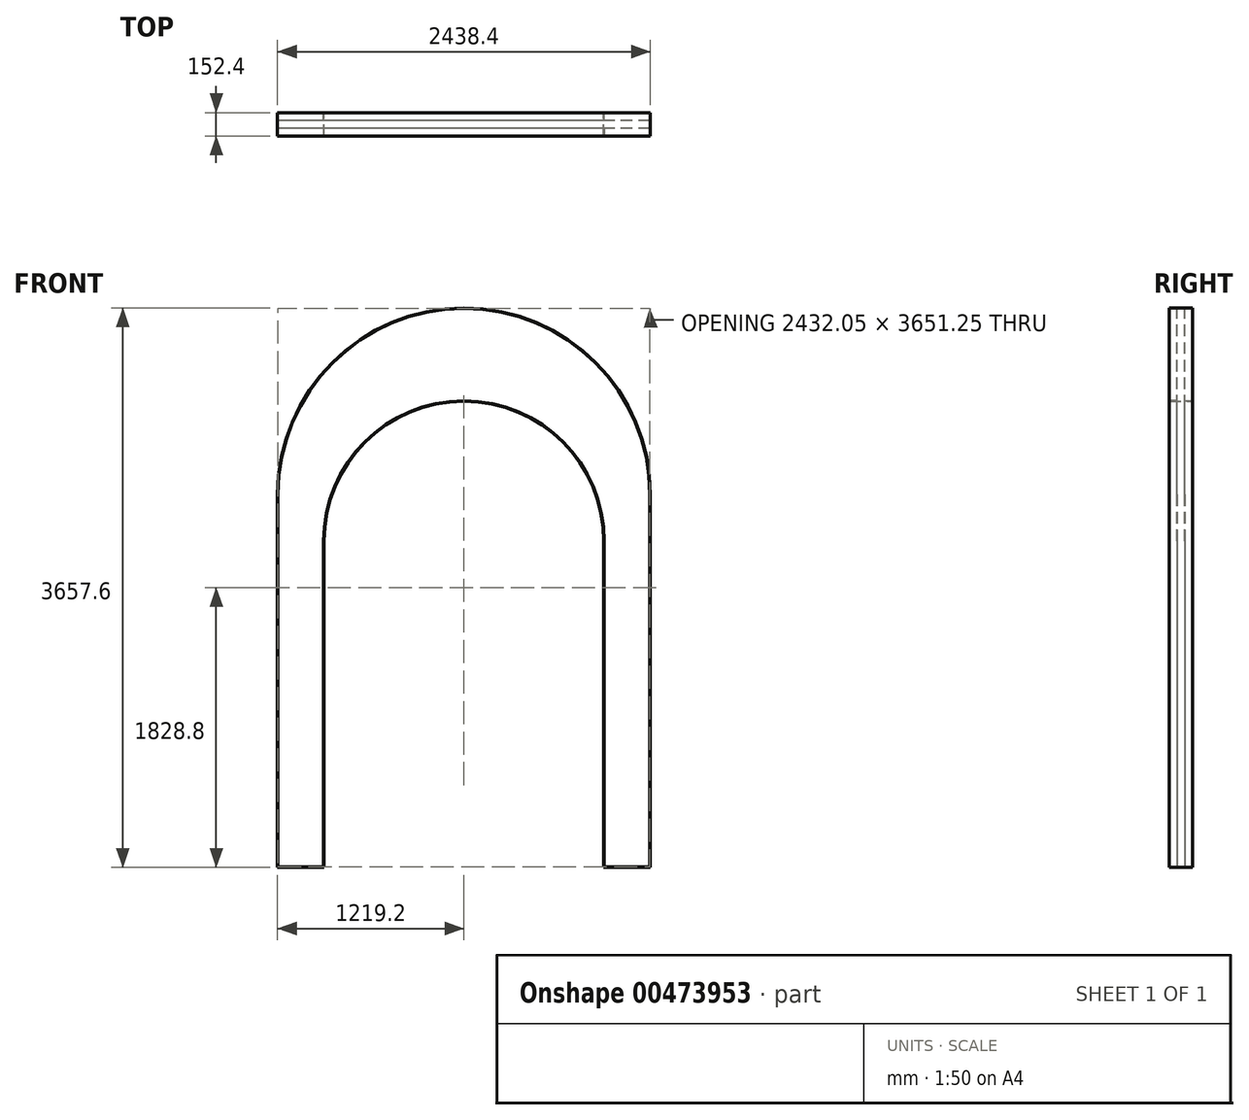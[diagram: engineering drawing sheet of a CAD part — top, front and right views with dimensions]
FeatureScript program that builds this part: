
annotation { "Feature Type Name" : "Feature", "Feature Type Description" : "" }
export const myFeature = defineFeature(function(context is Context, id is Id, definition is map)
    precondition{}
    {
        {
            var Q0;
            Q0=qCreatedBy(makeId("Front.planeOp"),FACE);
            var sketch = newSketch(context, id + "F0", { "sketchPlane" : qUnion([Q0])});
            skLineSegment(sketch, "E0", {"start": v(-1219.2, 0) * mm, "end": v(-1219.2, 2438.4) * mm});
            skLineSegment(sketch, "E1", {"start": v(1219.2, 2438.4) * mm, "end": v(1219.2, 0) * mm});
            skLineSegment(sketch, "E2", {"start": v(1219.2, 0) * mm, "end": v(0, 0) * mm});
            skLineSegment(sketch, "E3", {"start": v(0, 0) * mm, "end": v(-1219.2, 0) * mm});
            skArc(sketch, "E4", {"start": v(-1219.2, 2438.4) * mm, "mid": v(0, 3657.6) * mm, "end": v(1219.2, 2438.4) * mm});
            skLineSegment(sketch, "E5", {"start": v(-914.4, 0) * mm, "end": v(-914.4, 2133.6) * mm});
            skArc(sketch, "E6", {"start": v(914.4, 2133.6) * mm, "mid": v(0, 3048) * mm, "end": v(-914.4, 2133.6) * mm});
            skLineSegment(sketch, "E7", {"start": v(914.4, 2133.6) * mm, "end": v(914.4, 0) * mm});
            skSolve(sketch);
        }
        {
            var Q0;
            {var subQ4=sQuery(id+"F0.wireOp",EDGE,"E0");Q0=makeQuery(id+"F0.imprint","IMPRINT",FACE,{"disambiguationData":[TD([[makeQuery(id+"F0.imprint","IMPRINT",EDGE,{"derivedFrom":subQ4}),-1.0]])]});}
            extrude(context, id + "F1", {"entities" : qUnion([Q0]), "depth" : 76.2 * mm, "offsetDistance" : 25.4 * mm});
        }
        {
            var Q0;
            Q0=makeQuery(id+"F1.opExtrude","CAP_FACE",FACE,{"disambiguationData":[OSD([sQuery(id+"F0.wireOp",EDGE,"E0"),sQuery(id+"F0.wireOp",EDGE,"E1"),sQuery(id+"F0.wireOp",EDGE,"E2"),sQuery(id+"F0.wireOp",EDGE,"E3"),sQuery(id+"F0.wireOp",EDGE,"E4"),sQuery(id+"F0.wireOp",EDGE,"E5"),sQuery(id+"F0.wireOp",EDGE,"E6"),sQuery(id+"F0.wireOp",EDGE,"E7")])],"isStart":false});
            var sketch = newSketch(context, id + "F2", { "sketchPlane" : qUnion([Q0])});
            skLineSegment(sketch, "E8.0", {"start": v(917.58, 2133.6) * mm, "end": v(917.58, 3.18) * mm});
            skLineSegment(sketch, "E8.1", {"start": v(1216.02, 3.18) * mm, "end": v(917.58, 3.18) * mm});
            skArc(sketch, "E8.2", {"start": v(917.58, 2133.6) * mm, "mid": v(0, 3051.17) * mm, "end": v(-917.58, 2133.6) * mm});
            skLineSegment(sketch, "E8.3", {"start": v(1216.02, 2438.4) * mm, "end": v(1216.02, 3.18) * mm});
            skLineSegment(sketch, "E8.4", {"start": v(-917.58, 3.18) * mm, "end": v(-917.58, 2133.6) * mm});
            skLineSegment(sketch, "E8.5", {"start": v(-917.58, 3.18) * mm, "end": v(-1216.02, 3.18) * mm});
            skLineSegment(sketch, "E8.6", {"start": v(-1216.02, 3.18) * mm, "end": v(-1216.03, 2438.4) * mm});
            skArc(sketch, "E8.7", {"start": v(-1216.03, 2438.4) * mm, "mid": v(0, 3654.43) * mm, "end": v(1216.03, 2438.4) * mm});
            skSolve(sketch);
        }
        {
            var Q0;
            Q0 = qSketchRegion(id + "F2", true);
            extrude(context, id + "F3", {"entities" : qUnion([Q0]), "operationType" : NewBodyOperationType.REMOVE, "oppositeDirection" : true, "depth" : 50.8 * mm, "offsetDistance" : 25.4 * mm});
        }
        {
            var Q0;
            Q0=makeQuery(id+"F1.opExtrude","SWEPT_BODY",BODY,{"disambiguationData":[OSD([sQuery(id+"F0.wireOp",EDGE,"E0"),sQuery(id+"F0.wireOp",EDGE,"E1"),sQuery(id+"F0.wireOp",EDGE,"E2"),sQuery(id+"F0.wireOp",EDGE,"E3"),sQuery(id+"F0.wireOp",EDGE,"E4"),sQuery(id+"F0.wireOp",EDGE,"E5"),sQuery(id+"F0.wireOp",EDGE,"E6"),sQuery(id+"F0.wireOp",EDGE,"E7")])]});
            var Q1;
            Q1=makeQuery(id+"F1.opExtrude","CAP_FACE",FACE,{"disambiguationData":[OSD([sQuery(id+"F0.wireOp",EDGE,"E0"),sQuery(id+"F0.wireOp",EDGE,"E1"),sQuery(id+"F0.wireOp",EDGE,"E2"),sQuery(id+"F0.wireOp",EDGE,"E3"),sQuery(id+"F0.wireOp",EDGE,"E4"),sQuery(id+"F0.wireOp",EDGE,"E5"),sQuery(id+"F0.wireOp",EDGE,"E6"),sQuery(id+"F0.wireOp",EDGE,"E7")])],"isStart":true});
            mirror(context, id + "F4", {"operationType" : NewBodyOperationType.ADD, "entities" : qUnion([Q0]), "mirrorPlane" : qUnion([Q1])});
        }
    });
